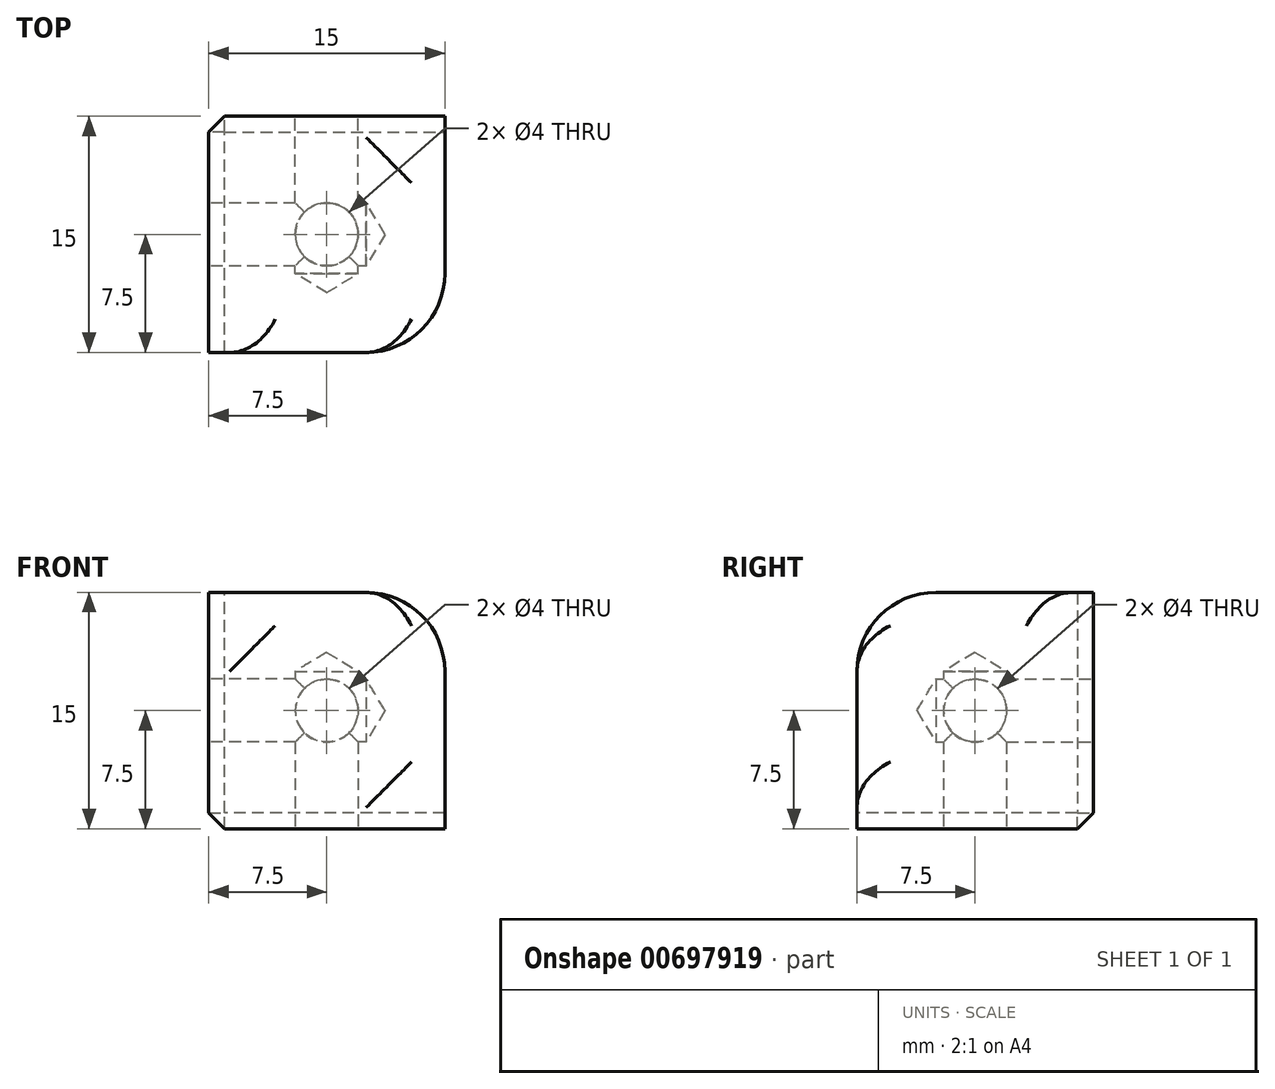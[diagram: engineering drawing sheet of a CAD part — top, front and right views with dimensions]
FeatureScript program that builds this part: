
annotation { "Feature Type Name" : "Feature", "Feature Type Description" : "" }
export const myFeature = defineFeature(function(context is Context, id is Id, definition is map)
    precondition{}
    {
        {
            var Q0;
            Q0=qCreatedBy(makeId("Front.planeOp"),FACE);
            var sketch = newSketch(context, id + "F0", { "sketchPlane" : qUnion([Q0])});
            skLineSegment(sketch, "E0.bottom", {"start": v(0, 0) * mm, "end": v(30, 0) * mm});
            skLineSegment(sketch, "E0.top", {"start": v(0, 30) * mm, "end": v(30, 30) * mm});
            skLineSegment(sketch, "E0.left", {"start": v(0, 0) * mm, "end": v(0, 30) * mm});
            skLineSegment(sketch, "E0.right", {"start": v(30, 0) * mm, "end": v(30, 30) * mm});
            skSolve(sketch);
        }
        {
            var Q0;
            Q0=makeQuery(id+"F0.imprint","IMPRINT",FACE,{"disambiguationData":[TD([[makeQuery(id+"F0.imprint","IMPRINT",EDGE,{"derivedFrom":sQuery(id+"F0.wireOp",EDGE,"E0.bottom")}),1.0]])]});
            extrude(context, id + "F1", {"entities" : qUnion([Q0]), "depth" : 30 * mm, "offsetDistance" : 25 * mm});
        }
        {
            var Q0;
            Q0=makeQuery(id+"F1.opExtrude","CAP_FACE",FACE,{"disambiguationData":[OSD([sQuery(id+"F0.wireOp",EDGE,"E0.bottom"),sQuery(id+"F0.wireOp",EDGE,"E0.top"),sQuery(id+"F0.wireOp",EDGE,"E0.left"),sQuery(id+"F0.wireOp",EDGE,"E0.right")])],"isStart":false});
            var sketch = newSketch(context, id + "F2", { "sketchPlane" : qUnion([Q0])});
            skLineSegment(sketch, "E1", {"start": v(0, 30) * mm, "end": v(30, 0) * mm});
            skLineSegment(sketch, "E2", {"start": v(30, 0) * mm, "end": v(30, 30) * mm});
            skLineSegment(sketch, "E3", {"start": v(30, 30) * mm, "end": v(0, 30) * mm});
            skSolve(sketch);
        }
        {
            var Q0;
            Q0=makeQuery(id+"F2.imprint","IMPRINT",FACE,{"disambiguationData":[TD([[makeQuery(id+"F2.imprint","IMPRINT",EDGE,{"derivedFrom":sQuery(id+"F2.wireOp",EDGE,"E1")}),1.0]])]});
            extrude(context, id + "F3", {"entities" : qUnion([Q0]), "operationType" : NewBodyOperationType.REMOVE, "endBound" : BoundingType.THROUGH_ALL, "oppositeDirection" : true, "depth" : 25 * mm, "offsetDistance" : 25 * mm});
        }
        {
            var Q0;
            Q0=makeQuery(id+"F1.opExtrude","SWEPT_FACE",FACE,{"disambiguationData":[OSD([sQuery(id+"F0.wireOp",EDGE,"E0.left")])]});
            var sketch = newSketch(context, id + "F4", { "sketchPlane" : qUnion([Q0])});
            skLineSegment(sketch, "E4", {"start": v(0, 30) * mm, "end": v(30, 30) * mm});
            skLineSegment(sketch, "E5", {"start": v(30, 30) * mm, "end": v(30, 0) * mm});
            skLineSegment(sketch, "E6", {"start": v(30, 0) * mm, "end": v(0, 30) * mm});
            skSolve(sketch);
        }
        {
            var Q0;
            Q0=makeQuery(id+"F4.imprint","IMPRINT",FACE,{"disambiguationData":[TD([[makeQuery(id+"F4.imprint","IMPRINT",EDGE,{"derivedFrom":sQuery(id+"F4.wireOp",EDGE,"E4")}),1.0]])]});
            extrude(context, id + "F5", {"entities" : qUnion([Q0]), "operationType" : NewBodyOperationType.REMOVE, "endBound" : BoundingType.THROUGH_ALL, "oppositeDirection" : true, "depth" : 25 * mm, "offsetDistance" : 25 * mm});
        }
        {
            var Q0;
            Q0=makeQuery(id+"F1.opExtrude","SWEPT_FACE",FACE,{"disambiguationData":[OSD([sQuery(id+"F0.wireOp",EDGE,"E0.bottom")])]});
            var sketch = newSketch(context, id + "F6", { "sketchPlane" : qUnion([Q0])});
            skLineSegment(sketch, "E7", {"start": v(0, 30) * mm, "end": v(30, 30) * mm});
            skLineSegment(sketch, "E8", {"start": v(30, 30) * mm, "end": v(30, 0) * mm});
            skLineSegment(sketch, "E9", {"start": v(30, 0) * mm, "end": v(0, 30) * mm});
            skSolve(sketch);
        }
        {
            var Q0;
            Q0=makeQuery(id+"F6.imprint","IMPRINT",FACE,{"disambiguationData":[TD([[makeQuery(id+"F6.imprint","IMPRINT",EDGE,{"derivedFrom":sQuery(id+"F6.wireOp",EDGE,"E7")}),-1.0]])]});
            extrude(context, id + "F7", {"entities" : qUnion([Q0]), "operationType" : NewBodyOperationType.REMOVE, "endBound" : BoundingType.THROUGH_ALL, "oppositeDirection" : true, "depth" : 25 * mm, "offsetDistance" : 25 * mm});
        }
        {
            var Q0;
            {var subQ0=sQuery(id+"F0.wireOp",EDGE,"E0.bottom");Q0=makeQuery(id+"F7.boolean.opBoolean","MERGE",VERTEX,{"derivedFrom":[makeQuery(id+"F1.opExtrude","CAP_VERTEX",VERTEX,{"disambiguationData":[OSD([subQ0,sQuery(id+"F0.wireOp",EDGE,"E0.right")])],"isStart":true}),makeQuery(id+"F7.opExtrude","CAP_VERTEX",VERTEX,{"disambiguationData":[OSD([subQ0,sQuery(id+"F6.wireOp",EDGE,"E8"),sQuery(id+"F6.wireOp",EDGE,"E9")])],"isStart":true})]});}
            var Q1;
            {var subQ0=sQuery(id+"F0.wireOp",EDGE,"E0.left");Q1=makeQuery(id+"F5.boolean.opBoolean","MERGE",VERTEX,{"derivedFrom":[makeQuery(id+"F1.opExtrude","CAP_VERTEX",VERTEX,{"disambiguationData":[OSD([sQuery(id+"F0.wireOp",EDGE,"E0.top"),subQ0])],"isStart":true}),makeQuery(id+"F5.opExtrude","CAP_VERTEX",VERTEX,{"disambiguationData":[OSD([subQ0,sQuery(id+"F4.wireOp",EDGE,"E4"),sQuery(id+"F4.wireOp",EDGE,"E6")])],"isStart":true})]});}
            var Q2;
            {var subQ0=sQuery(id+"F0.wireOp",EDGE,"E0.left");var subQ1=sQuery(id+"F0.wireOp",EDGE,"E0.bottom");Q2=makeQuery(id+"F7.boolean.opBoolean","MERGE",VERTEX,{"derivedFrom":[makeQuery(id+"F5.boolean.opBoolean","MERGE",VERTEX,{"derivedFrom":[makeQuery(id+"F1.opExtrude","CAP_VERTEX",VERTEX,{"disambiguationData":[OSD([subQ1,subQ0])],"isStart":false}),makeQuery(id+"F5.opExtrude","CAP_VERTEX",VERTEX,{"disambiguationData":[OSD([subQ1,subQ0,sQuery(id+"F4.wireOp",EDGE,"E5"),sQuery(id+"F4.wireOp",EDGE,"E6")])],"isStart":true})]}),makeQuery(id+"F7.opExtrude","CAP_VERTEX",VERTEX,{"disambiguationData":[OSD([subQ1,subQ0,sQuery(id+"F6.wireOp",EDGE,"E7"),sQuery(id+"F6.wireOp",EDGE,"E9")])],"isStart":true})]});}
            cPlane(context, id + "F8", {"entities" : qUnion([Q0, Q1, Q2]), "cplaneType" : CPlaneType.THREE_POINT, "offset" : 25 * mm, "width" : 150 * mm, "height" : 150 * mm});
        }
        {
            var Q0;
            Q0=qCreatedBy(id+"F8.planeOp",FACE);
            var sketch = newSketch(context, id + "F9", { "sketchPlane" : qUnion([Q0])});
            skLineSegment(sketch, "E10.bottom", {"start": v(27.01, -22.9) * mm, "end": v(-16.5, -22.9) * mm});
            skLineSegment(sketch, "E10.top", {"start": v(27.01, 27.56) * mm, "end": v(-16.5, 27.56) * mm});
            skLineSegment(sketch, "E10.left", {"start": v(27.01, -22.9) * mm, "end": v(27.01, 27.56) * mm});
            skLineSegment(sketch, "E10.right", {"start": v(-16.5, -22.9) * mm, "end": v(-16.5, 27.56) * mm});
            skSolve(sketch);
        }
        {
            var Q0;
            Q0 = qSketchRegion(id + "F9", true);
            extrude(context, id + "F10", {"entities" : qUnion([Q0]), "operationType" : NewBodyOperationType.REMOVE, "endBound" : BoundingType.THROUGH_ALL, "oppositeDirection" : true, "depth" : 25 * mm, "offsetDistance" : 25 * mm});
        }
        {
            var Q0;
            Q0=makeQuery(id+"F1.opExtrude","SWEPT_FACE",FACE,{"disambiguationData":[OSD([sQuery(id+"F0.wireOp",EDGE,"E0.left")])]});
            var sketch = newSketch(context, id + "F11", { "sketchPlane" : qUnion([Q0])});
            skPoint(sketch, "E11", {"position": v(7.5, 7.5) * mm});
            skSolve(sketch);
        }
        {
            var Q0;
            Q0=sQuery(id+"F11.wireOp",VERTEX,"E11");
            var Q1;
            Q1=makeQuery(id+"F1.opExtrude","SWEPT_BODY",BODY,{"disambiguationData":[OSD([sQuery(id+"F0.wireOp",EDGE,"E0.bottom"),sQuery(id+"F0.wireOp",EDGE,"E0.top"),sQuery(id+"F0.wireOp",EDGE,"E0.left"),sQuery(id+"F0.wireOp",EDGE,"E0.right")])]});
            hole(context, id + "F12", {"style" : HoleStyle.SIMPLE, "endStyle" : HoleEndStyle.BLIND, "holeDiameter" : 4 * mm, "majorDiameter" : 5 * mm, "holeDepth" : 10 * mm, "isTappedThrough" : true, "tappedDepth" : 12 * mm, "tapClearance" : 3, "locations" : qUnion([Q0]), "scope" : qUnion([Q1])});
        }
        {
            var Q0;
            Q0=makeQuery(id+"F1.opExtrude","CAP_FACE",FACE,{"disambiguationData":[OSD([sQuery(id+"F0.wireOp",EDGE,"E0.bottom"),sQuery(id+"F0.wireOp",EDGE,"E0.top"),sQuery(id+"F0.wireOp",EDGE,"E0.left"),sQuery(id+"F0.wireOp",EDGE,"E0.right")])],"isStart":true});
            var sketch = newSketch(context, id + "F13", { "sketchPlane" : qUnion([Q0])});
            skPoint(sketch, "E12", {"position": v(-7.5, 7.5) * mm});
            skSolve(sketch);
        }
        {
            var Q0;
            Q0=sQuery(id+"F13.wireOp",VERTEX,"E12");
            var Q1;
            Q1=makeQuery(id+"F1.opExtrude","SWEPT_BODY",BODY,{"disambiguationData":[OSD([sQuery(id+"F0.wireOp",EDGE,"E0.bottom"),sQuery(id+"F0.wireOp",EDGE,"E0.top"),sQuery(id+"F0.wireOp",EDGE,"E0.left"),sQuery(id+"F0.wireOp",EDGE,"E0.right")])]});
            hole(context, id + "F14", {"style" : HoleStyle.SIMPLE, "endStyle" : HoleEndStyle.BLIND, "holeDiameter" : 4 * mm, "majorDiameter" : 5 * mm, "holeDepth" : 10 * mm, "isTappedThrough" : true, "tappedDepth" : 12 * mm, "tapClearance" : 3, "locations" : qUnion([Q0]), "scope" : qUnion([Q1])});
        }
        {
            var Q0;
            Q0=makeQuery(id+"F1.opExtrude","SWEPT_FACE",FACE,{"disambiguationData":[OSD([sQuery(id+"F0.wireOp",EDGE,"E0.bottom")])]});
            var sketch = newSketch(context, id + "F15", { "sketchPlane" : qUnion([Q0])});
            skPoint(sketch, "E13", {"position": v(7.5, 7.5) * mm});
            skSolve(sketch);
        }
        {
            var Q0;
            Q0=sQuery(id+"F15.wireOp",VERTEX,"E13");
            var Q1;
            Q1=makeQuery(id+"F1.opExtrude","SWEPT_BODY",BODY,{"disambiguationData":[OSD([sQuery(id+"F0.wireOp",EDGE,"E0.bottom"),sQuery(id+"F0.wireOp",EDGE,"E0.top"),sQuery(id+"F0.wireOp",EDGE,"E0.left"),sQuery(id+"F0.wireOp",EDGE,"E0.right")])]});
            hole(context, id + "F16", {"style" : HoleStyle.SIMPLE, "endStyle" : HoleEndStyle.BLIND, "holeDiameter" : 4 * mm, "majorDiameter" : 5 * mm, "holeDepth" : 10 * mm, "isTappedThrough" : true, "tappedDepth" : 12 * mm, "tapClearance" : 3, "locations" : qUnion([Q0]), "scope" : qUnion([Q1])});
        }
        {
            var Q0;
            Q0=makeQuery(id+"F1.opExtrude","SWEPT_EDGE",EDGE,{"disambiguationData":[OSD([sQuery(id+"F0.wireOp",EDGE,"E0.bottom"),sQuery(id+"F0.wireOp",EDGE,"E0.left")])]});
            var Q1;
            Q1=makeQuery(id+"F1.opExtrude","CAP_EDGE",EDGE,{"disambiguationData":[OSD([sQuery(id+"F0.wireOp",EDGE,"E0.left")])],"isStart":true});
            var Q2;
            Q2=makeQuery(id+"F1.opExtrude","CAP_EDGE",EDGE,{"disambiguationData":[OSD([sQuery(id+"F0.wireOp",EDGE,"E0.bottom")])],"isStart":true});
            chamfer(context, id + "F17", {"entities" : qUnion([Q0, Q1, Q2]), "width" : 1 * mm, "tangentPropagation" : true});
        }
        {
            var Q0;
            Q0=qCreatedBy(makeId("Top.planeOp"),FACE);
            var sketch = newSketch(context, id + "F18", { "sketchPlane" : qUnion([Q0])});
            skLineSegment(sketch, "E14.bottom", {"start": v(47.57, -37.78) * mm, "end": v(-14.14, -37.78) * mm});
            skLineSegment(sketch, "E14.top", {"start": v(47.57, -15) * mm, "end": v(-14.14, -15) * mm});
            skLineSegment(sketch, "E14.left", {"start": v(47.57, -37.78) * mm, "end": v(47.57, -15) * mm});
            skLineSegment(sketch, "E14.right", {"start": v(-14.14, -37.78) * mm, "end": v(-14.14, -15) * mm});
            skSolve(sketch);
        }
        {
            var Q0;
            Q0 = qSketchRegion(id + "F18", true);
            extrude(context, id + "F19", {"entities" : qUnion([Q0]), "operationType" : NewBodyOperationType.REMOVE, "depth" : 25 * mm, "offsetDistance" : 25 * mm});
        }
        {
            var Q0;
            Q0=qCreatedBy(makeId("Right.planeOp"),FACE);
            var sketch = newSketch(context, id + "F20", { "sketchPlane" : qUnion([Q0])});
            skLineSegment(sketch, "E15.bottom", {"start": v(-34.33, 41.25) * mm, "end": v(45.14, 41.25) * mm});
            skLineSegment(sketch, "E15.top", {"start": v(-34.33, 15) * mm, "end": v(45.14, 15) * mm});
            skLineSegment(sketch, "E15.left", {"start": v(-34.33, 41.25) * mm, "end": v(-34.33, 15) * mm});
            skLineSegment(sketch, "E15.right", {"start": v(45.14, 41.25) * mm, "end": v(45.14, 15) * mm});
            skSolve(sketch);
        }
        {
            var Q0;
            Q0=makeQuery(id+"F20.imprint","IMPRINT",FACE,{"disambiguationData":[TD([[makeQuery(id+"F20.imprint","IMPRINT",EDGE,{"derivedFrom":sQuery(id+"F20.wireOp",EDGE,"E15.bottom")}),-1.0]])]});
            extrude(context, id + "F21", {"entities" : qUnion([Q0]), "operationType" : NewBodyOperationType.REMOVE, "depth" : 25 * mm, "offsetDistance" : 25 * mm});
        }
        {
            var Q0;
            Q0=qCreatedBy(makeId("Front.planeOp"),FACE);
            var sketch = newSketch(context, id + "F22", { "sketchPlane" : qUnion([Q0])});
            skLineSegment(sketch, "E16.bottom", {"start": v(30.6, 19.87) * mm, "end": v(15, 19.87) * mm});
            skLineSegment(sketch, "E16.top", {"start": v(30.6, -27.24) * mm, "end": v(15, -27.24) * mm});
            skLineSegment(sketch, "E16.left", {"start": v(30.6, 19.87) * mm, "end": v(30.6, -27.24) * mm});
            skLineSegment(sketch, "E16.right", {"start": v(15, 19.87) * mm, "end": v(15, -27.24) * mm});
            skSolve(sketch);
        }
        {
            var Q0;
            Q0=makeQuery(id+"F22.imprint","IMPRINT",FACE,{"disambiguationData":[TD([[makeQuery(id+"F22.imprint","IMPRINT",EDGE,{"derivedFrom":sQuery(id+"F22.wireOp",EDGE,"E16.bottom")}),1.0]])]});
            extrude(context, id + "F23", {"entities" : qUnion([Q0]), "operationType" : NewBodyOperationType.REMOVE, "depth" : 25 * mm, "offsetDistance" : 25 * mm});
        }
        {
            var Q0;
            Q0=makeQuery(id+"F19.boolean.opBoolean","INTERSECT",EDGE,{"disambiguationData":[OD(1.0)],"derivedFrom":[makeQuery(id+"F10.boolean.opBoolean","COPY",FACE,{"derivedFrom":makeQuery(id+"F10.opExtrude","CAP_FACE",FACE,{"disambiguationData":[OSD([sQuery(id+"F9.wireOp",EDGE,"E10.bottom"),sQuery(id+"F9.wireOp",EDGE,"E10.top"),sQuery(id+"F9.wireOp",EDGE,"E10.left"),sQuery(id+"F9.wireOp",EDGE,"E10.right")])],"isStart":true})}),makeQuery(id+"F19.opExtrude","SWEPT_FACE",FACE,{"disambiguationData":[OSD([sQuery(id+"F18.wireOp",EDGE,"E14.top")])]})]});
            var Q1;
            Q1=makeQuery(id+"F19.boolean.opBoolean","INTERSECT",EDGE,{"disambiguationData":[OD(0.0)],"derivedFrom":[makeQuery(id+"F10.boolean.opBoolean","COPY",FACE,{"derivedFrom":makeQuery(id+"F10.opExtrude","CAP_FACE",FACE,{"disambiguationData":[OSD([sQuery(id+"F9.wireOp",EDGE,"E10.bottom"),sQuery(id+"F9.wireOp",EDGE,"E10.top"),sQuery(id+"F9.wireOp",EDGE,"E10.left"),sQuery(id+"F9.wireOp",EDGE,"E10.right")])],"isStart":true})}),makeQuery(id+"F19.opExtrude","SWEPT_FACE",FACE,{"disambiguationData":[OSD([sQuery(id+"F18.wireOp",EDGE,"E14.top")])]})]});
            fillet(context, id + "F24", {"entities" : qUnion([Q0, Q1]), "radius" : 5 * mm, "tangentPropagation" : true, "allowEdgeOverflow" : false});
        }
        {
            var Q0;
            Q0=makeQuery(id+"F21.boolean.opBoolean","INTERSECT",EDGE,{"disambiguationData":[OD(0.0)],"derivedFrom":[makeQuery(id+"F10.boolean.opBoolean","COPY",FACE,{"derivedFrom":makeQuery(id+"F10.opExtrude","CAP_FACE",FACE,{"disambiguationData":[OSD([sQuery(id+"F9.wireOp",EDGE,"E10.bottom"),sQuery(id+"F9.wireOp",EDGE,"E10.top"),sQuery(id+"F9.wireOp",EDGE,"E10.left"),sQuery(id+"F9.wireOp",EDGE,"E10.right")])],"isStart":true})}),makeQuery(id+"F21.opExtrude","SWEPT_FACE",FACE,{"disambiguationData":[OSD([sQuery(id+"F20.wireOp",EDGE,"E15.top")])]})]});
            var Q1;
            Q1=makeQuery(id+"F21.boolean.opBoolean","INTERSECT",EDGE,{"disambiguationData":[OD(1.0)],"derivedFrom":[makeQuery(id+"F10.boolean.opBoolean","COPY",FACE,{"derivedFrom":makeQuery(id+"F10.opExtrude","CAP_FACE",FACE,{"disambiguationData":[OSD([sQuery(id+"F9.wireOp",EDGE,"E10.bottom"),sQuery(id+"F9.wireOp",EDGE,"E10.top"),sQuery(id+"F9.wireOp",EDGE,"E10.left"),sQuery(id+"F9.wireOp",EDGE,"E10.right")])],"isStart":true})}),makeQuery(id+"F21.opExtrude","SWEPT_FACE",FACE,{"disambiguationData":[OSD([sQuery(id+"F20.wireOp",EDGE,"E15.top")])]})]});
            var Q2;
            Q2=makeQuery(id+"F24.opFillet","BLEND_EDGE",EDGE,{"blendedFrom":[makeQuery(id+"F19.boolean.opBoolean","INTERSECT",EDGE,{"disambiguationData":[OD(1.0)],"derivedFrom":[makeQuery(id+"F10.boolean.opBoolean","COPY",FACE,{"derivedFrom":makeQuery(id+"F10.opExtrude","CAP_FACE",FACE,{"disambiguationData":[OSD([sQuery(id+"F9.wireOp",EDGE,"E10.bottom"),sQuery(id+"F9.wireOp",EDGE,"E10.top"),sQuery(id+"F9.wireOp",EDGE,"E10.left"),sQuery(id+"F9.wireOp",EDGE,"E10.right")])],"isStart":true})}),makeQuery(id+"F19.opExtrude","SWEPT_FACE",FACE,{"disambiguationData":[OSD([sQuery(id+"F18.wireOp",EDGE,"E14.top")])]})]}),makeQuery(id+"F21.boolean.opBoolean","COPY",FACE,{"derivedFrom":makeQuery(id+"F21.opExtrude","SWEPT_FACE",FACE,{"disambiguationData":[OSD([sQuery(id+"F20.wireOp",EDGE,"E15.top")])]})})],"blendedInto":[makeQuery(id+"F21.boolean.opBoolean","COPY",FACE,{"derivedFrom":makeQuery(id+"F21.opExtrude","SWEPT_FACE",FACE,{"disambiguationData":[OSD([sQuery(id+"F20.wireOp",EDGE,"E15.top")])]})})]});
            fillet(context, id + "F25", {"entities" : qUnion([Q0, Q1, Q2]), "radius" : 5 * mm, "tangentPropagation" : true, "allowEdgeOverflow" : false});
        }
        {
            var Q0;
            Q0=makeQuery(id+"F24.opFillet","BLEND_EDGE",EDGE,{"blendedFrom":[makeQuery(id+"F19.boolean.opBoolean","INTERSECT",EDGE,{"disambiguationData":[OD(1.0)],"derivedFrom":[makeQuery(id+"F10.boolean.opBoolean","COPY",FACE,{"derivedFrom":makeQuery(id+"F10.opExtrude","CAP_FACE",FACE,{"disambiguationData":[OSD([sQuery(id+"F9.wireOp",EDGE,"E10.bottom"),sQuery(id+"F9.wireOp",EDGE,"E10.top"),sQuery(id+"F9.wireOp",EDGE,"E10.left"),sQuery(id+"F9.wireOp",EDGE,"E10.right")])],"isStart":true})}),makeQuery(id+"F19.opExtrude","SWEPT_FACE",FACE,{"disambiguationData":[OSD([sQuery(id+"F18.wireOp",EDGE,"E14.top")])]})]}),makeQuery(id+"F23.boolean.opBoolean","COPY",FACE,{"derivedFrom":makeQuery(id+"F23.opExtrude","SWEPT_FACE",FACE,{"disambiguationData":[OSD([sQuery(id+"F22.wireOp",EDGE,"E16.right")])]})})],"blendedInto":[makeQuery(id+"F23.boolean.opBoolean","COPY",FACE,{"derivedFrom":makeQuery(id+"F23.opExtrude","SWEPT_FACE",FACE,{"disambiguationData":[OSD([sQuery(id+"F22.wireOp",EDGE,"E16.right")])]})})]});
            var Q1;
            Q1=makeQuery(id+"F23.boolean.opBoolean","INTERSECT",EDGE,{"disambiguationData":[OD(0.0)],"derivedFrom":[makeQuery(id+"F10.boolean.opBoolean","COPY",FACE,{"derivedFrom":makeQuery(id+"F10.opExtrude","CAP_FACE",FACE,{"disambiguationData":[OSD([sQuery(id+"F9.wireOp",EDGE,"E10.bottom"),sQuery(id+"F9.wireOp",EDGE,"E10.top"),sQuery(id+"F9.wireOp",EDGE,"E10.left"),sQuery(id+"F9.wireOp",EDGE,"E10.right")])],"isStart":true})}),makeQuery(id+"F23.opExtrude","SWEPT_FACE",FACE,{"disambiguationData":[OSD([sQuery(id+"F22.wireOp",EDGE,"E16.right")])]})]});
            var Q2;
            Q2=makeQuery(id+"F23.boolean.opBoolean","INTERSECT",EDGE,{"disambiguationData":[OD(1.0)],"derivedFrom":[makeQuery(id+"F10.boolean.opBoolean","COPY",FACE,{"derivedFrom":makeQuery(id+"F10.opExtrude","CAP_FACE",FACE,{"disambiguationData":[OSD([sQuery(id+"F9.wireOp",EDGE,"E10.bottom"),sQuery(id+"F9.wireOp",EDGE,"E10.top"),sQuery(id+"F9.wireOp",EDGE,"E10.left"),sQuery(id+"F9.wireOp",EDGE,"E10.right")])],"isStart":true})}),makeQuery(id+"F23.opExtrude","SWEPT_FACE",FACE,{"disambiguationData":[OSD([sQuery(id+"F22.wireOp",EDGE,"E16.right")])]})]});
            var Q3;
            Q3=makeQuery(id+"F25.opFillet","BLEND_EDGE",EDGE,{"blendedFrom":[makeQuery(id+"F21.boolean.opBoolean","INTERSECT",EDGE,{"disambiguationData":[OD(1.0)],"derivedFrom":[makeQuery(id+"F10.boolean.opBoolean","COPY",FACE,{"derivedFrom":makeQuery(id+"F10.opExtrude","CAP_FACE",FACE,{"disambiguationData":[OSD([sQuery(id+"F9.wireOp",EDGE,"E10.bottom"),sQuery(id+"F9.wireOp",EDGE,"E10.top"),sQuery(id+"F9.wireOp",EDGE,"E10.left"),sQuery(id+"F9.wireOp",EDGE,"E10.right")])],"isStart":true})}),makeQuery(id+"F21.opExtrude","SWEPT_FACE",FACE,{"disambiguationData":[OSD([sQuery(id+"F20.wireOp",EDGE,"E15.top")])]})]}),makeQuery(id+"F23.boolean.opBoolean","COPY",FACE,{"derivedFrom":makeQuery(id+"F23.opExtrude","SWEPT_FACE",FACE,{"disambiguationData":[OSD([sQuery(id+"F22.wireOp",EDGE,"E16.right")])]})})],"blendedInto":[makeQuery(id+"F23.boolean.opBoolean","COPY",FACE,{"derivedFrom":makeQuery(id+"F23.opExtrude","SWEPT_FACE",FACE,{"disambiguationData":[OSD([sQuery(id+"F22.wireOp",EDGE,"E16.right")])]})})]});
            fillet(context, id + "F26", {"entities" : qUnion([Q0, Q1, Q2, Q3]), "radius" : 5 * mm, "tangentPropagation" : true, "allowEdgeOverflow" : false});
        }
    });
